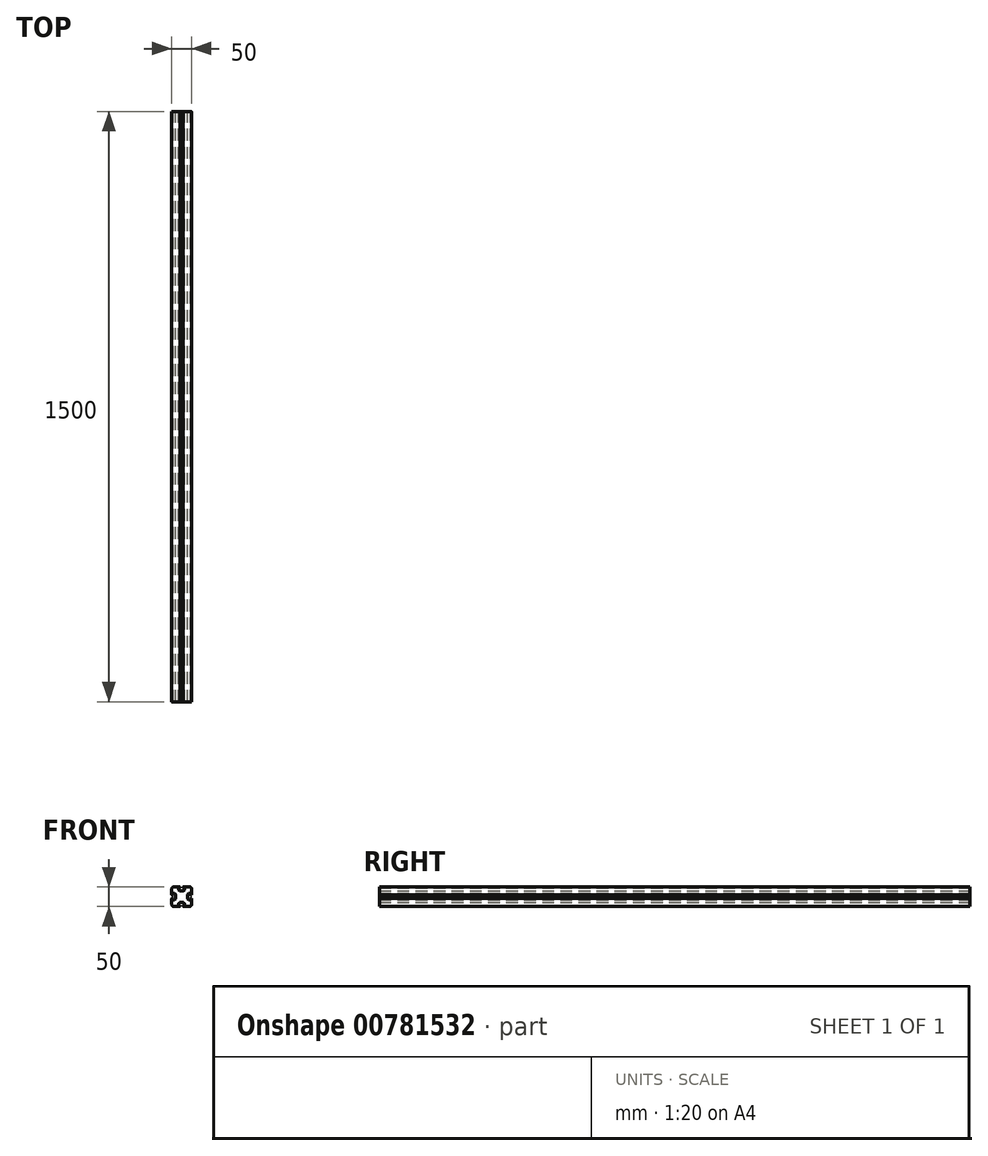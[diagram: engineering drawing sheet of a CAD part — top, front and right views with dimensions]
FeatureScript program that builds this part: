
annotation { "Feature Type Name" : "Feature", "Feature Type Description" : "" }
export const myFeature = defineFeature(function(context is Context, id is Id, definition is map)
    precondition{}
    {
        {
            var Q0;
            Q0=qCreatedBy(makeId("Front.planeOp"),FACE);
            var sketch = newSketch(context, id + "F0", { "sketchPlane" : qUnion([Q0])});
            skLineSegment(sketch, "E0", {"start": v(-15, 0) * mm, "end": v(-15, 5) * mm});
            skLineSegment(sketch, "E1", {"start": v(-15, 5) * mm, "end": v(-18, 8) * mm});
            skLineSegment(sketch, "E2", {"start": v(-18, 8) * mm, "end": v(-22, 8) * mm});
            skLineSegment(sketch, "E3", {"start": v(-22, 8) * mm, "end": v(-22, 4) * mm});
            skLineSegment(sketch, "E4", {"start": v(-22, 4) * mm, "end": v(-25, 4) * mm});
            skLineSegment(sketch, "E5", {"start": v(-25, 4) * mm, "end": v(-25, 25) * mm});
            skLineSegment(sketch, "E6", {"start": v(-25, 25) * mm, "end": v(0, 0) * mm, "construction": true});
            skLineSegment(sketch, "E7.MirrorCS", {"start": v(-4, 25) * mm, "end": v(-25, 25) * mm});
            skLineSegment(sketch, "E8.MirrorCS", {"start": v(-4, 22) * mm, "end": v(-4, 25) * mm});
            skLineSegment(sketch, "E9.MirrorCS", {"start": v(-8, 18) * mm, "end": v(-8, 22) * mm});
            skLineSegment(sketch, "E10.MirrorCS", {"start": v(-5, 15) * mm, "end": v(-8, 18) * mm});
            skLineSegment(sketch, "E11.MirrorCS", {"start": v(-8, 22) * mm, "end": v(-4, 22) * mm});
            skLineSegment(sketch, "E12.MirrorCS", {"start": v(0, 15) * mm, "end": v(-5, 15) * mm});
            skLineSegment(sketch, "E13.1.0", {"start": v(-25, -4) * mm, "end": v(-25, -25) * mm});
            skLineSegment(sketch, "E13.1.1", {"start": v(-22, -4) * mm, "end": v(-25, -4) * mm});
            skLineSegment(sketch, "E13.1.2", {"start": v(-22, -8) * mm, "end": v(-22, -4) * mm});
            skLineSegment(sketch, "E13.1.3", {"start": v(-18, -8) * mm, "end": v(-22, -8) * mm});
            skLineSegment(sketch, "E13.1.4", {"start": v(-15, 0) * mm, "end": v(-15, -5) * mm});
            skLineSegment(sketch, "E13.1.5", {"start": v(-15, -5) * mm, "end": v(-18, -8) * mm});
            skLineSegment(sketch, "E13.1.6", {"start": v(-8, -18) * mm, "end": v(-8, -22) * mm});
            skLineSegment(sketch, "E13.1.7", {"start": v(-5, -15) * mm, "end": v(-8, -18) * mm});
            skLineSegment(sketch, "E13.1.8", {"start": v(0, -15) * mm, "end": v(-5, -15) * mm});
            skLineSegment(sketch, "E13.1.9", {"start": v(-4, -22) * mm, "end": v(-4, -25) * mm});
            skLineSegment(sketch, "E13.1.10", {"start": v(-4, -25) * mm, "end": v(-25, -25) * mm});
            skLineSegment(sketch, "E13.1.11", {"start": v(-8, -22) * mm, "end": v(-4, -22) * mm});
            skLineSegment(sketch, "E13.2.0", {"start": v(4, -25) * mm, "end": v(25, -25) * mm});
            skLineSegment(sketch, "E13.2.1", {"start": v(4, -22) * mm, "end": v(4, -25) * mm});
            skLineSegment(sketch, "E13.2.2", {"start": v(8, -22) * mm, "end": v(4, -22) * mm});
            skLineSegment(sketch, "E13.2.3", {"start": v(8, -18) * mm, "end": v(8, -22) * mm});
            skLineSegment(sketch, "E13.2.4", {"start": v(0, -15) * mm, "end": v(5, -15) * mm});
            skLineSegment(sketch, "E13.2.5", {"start": v(5, -15) * mm, "end": v(8, -18) * mm});
            skLineSegment(sketch, "E13.2.6", {"start": v(18, -8) * mm, "end": v(22, -8) * mm});
            skLineSegment(sketch, "E13.2.7", {"start": v(15, -5) * mm, "end": v(18, -8) * mm});
            skLineSegment(sketch, "E13.2.8", {"start": v(15, 0) * mm, "end": v(15, -5) * mm});
            skLineSegment(sketch, "E13.2.9", {"start": v(22, -4) * mm, "end": v(25, -4) * mm});
            skLineSegment(sketch, "E13.2.10", {"start": v(25, -4) * mm, "end": v(25, -25) * mm});
            skLineSegment(sketch, "E13.2.11", {"start": v(22, -8) * mm, "end": v(22, -4) * mm});
            skLineSegment(sketch, "E13.3.0", {"start": v(25, 4) * mm, "end": v(25, 25) * mm});
            skLineSegment(sketch, "E13.3.1", {"start": v(22, 4) * mm, "end": v(25, 4) * mm});
            skLineSegment(sketch, "E13.3.2", {"start": v(22, 8) * mm, "end": v(22, 4) * mm});
            skLineSegment(sketch, "E13.3.3", {"start": v(18, 8) * mm, "end": v(22, 8) * mm});
            skLineSegment(sketch, "E13.3.4", {"start": v(15, 0) * mm, "end": v(15, 5) * mm});
            skLineSegment(sketch, "E13.3.5", {"start": v(15, 5) * mm, "end": v(18, 8) * mm});
            skLineSegment(sketch, "E13.3.6", {"start": v(8, 18) * mm, "end": v(8, 22) * mm});
            skLineSegment(sketch, "E13.3.7", {"start": v(5, 15) * mm, "end": v(8, 18) * mm});
            skLineSegment(sketch, "E13.3.8", {"start": v(0, 15) * mm, "end": v(5, 15) * mm});
            skLineSegment(sketch, "E13.3.9", {"start": v(4, 22) * mm, "end": v(4, 25) * mm});
            skLineSegment(sketch, "E13.3.10", {"start": v(4, 25) * mm, "end": v(25, 25) * mm});
            skLineSegment(sketch, "E13.3.11", {"start": v(8, 22) * mm, "end": v(4, 22) * mm});
            skPoint(sketch, "E13.center", {"position": v(0, 0) * mm});
            skSolve(sketch);
        }
        {
            var Q0;
            Q0=makeQuery(id+"F0.imprint","IMPRINT",FACE,{"disambiguationData":[TD([[makeQuery(id+"F0.imprint","IMPRINT",EDGE,{"derivedFrom":sQuery(id+"F0.wireOp",EDGE,"E0")}),-1.0]])]});
            extrude(context, id + "F1", {"entities" : qUnion([Q0]), "depth" : 1500 * mm, "offsetDistance" : 25 * mm});
        }
        {
            var Q0;
            Q0=makeQuery(id+"F1.opExtrude","SWEPT_EDGE",EDGE,{"disambiguationData":[OSD([sQuery(id+"F0.wireOp",EDGE,"E13.3.0"),sQuery(id+"F0.wireOp",EDGE,"E13.3.10")])]});
            var Q1;
            Q1=makeQuery(id+"F1.opExtrude","SWEPT_EDGE",EDGE,{"disambiguationData":[OSD([sQuery(id+"F0.wireOp",EDGE,"E13.2.0"),sQuery(id+"F0.wireOp",EDGE,"E13.2.10")])]});
            var Q2;
            Q2=makeQuery(id+"F1.opExtrude","SWEPT_EDGE",EDGE,{"disambiguationData":[OSD([sQuery(id+"F0.wireOp",EDGE,"E5"),sQuery(id+"F0.wireOp",EDGE,"E7.MirrorCS")])]});
            var Q3;
            Q3=makeQuery(id+"F1.opExtrude","SWEPT_EDGE",EDGE,{"disambiguationData":[OSD([sQuery(id+"F0.wireOp",EDGE,"E13.1.0"),sQuery(id+"F0.wireOp",EDGE,"E13.1.10")])]});
            fillet(context, id + "F2", {"entities" : qUnion([Q0, Q1, Q2, Q3]), "radius" : 5 * mm, "tangentPropagation" : true, "allowEdgeOverflow" : false});
        }
        {
            var Q0;
            Q0=makeQuery(id+"F1.opExtrude","SWEPT_EDGE",EDGE,{"disambiguationData":[OSD([sQuery(id+"F0.wireOp",EDGE,"E7.MirrorCS"),sQuery(id+"F0.wireOp",EDGE,"E8.MirrorCS")])]});
            var Q1;
            Q1=makeQuery(id+"F1.opExtrude","SWEPT_EDGE",EDGE,{"disambiguationData":[OSD([sQuery(id+"F0.wireOp",EDGE,"E13.3.9"),sQuery(id+"F0.wireOp",EDGE,"E13.3.10")])]});
            var Q2;
            Q2=makeQuery(id+"F1.opExtrude","SWEPT_EDGE",EDGE,{"disambiguationData":[OSD([sQuery(id+"F0.wireOp",EDGE,"E13.3.9"),sQuery(id+"F0.wireOp",EDGE,"E13.3.11")])]});
            var Q3;
            Q3=makeQuery(id+"F1.opExtrude","SWEPT_EDGE",EDGE,{"disambiguationData":[OSD([sQuery(id+"F0.wireOp",EDGE,"E13.3.6"),sQuery(id+"F0.wireOp",EDGE,"E13.3.7")])]});
            var Q4;
            Q4=makeQuery(id+"F1.opExtrude","SWEPT_EDGE",EDGE,{"disambiguationData":[OSD([sQuery(id+"F0.wireOp",EDGE,"E13.3.7"),sQuery(id+"F0.wireOp",EDGE,"E13.3.8")])]});
            var Q5;
            Q5=makeQuery(id+"F1.opExtrude","SWEPT_EDGE",EDGE,{"disambiguationData":[OSD([sQuery(id+"F0.wireOp",EDGE,"E9.MirrorCS"),sQuery(id+"F0.wireOp",EDGE,"E10.MirrorCS")])]});
            var Q6;
            Q6=makeQuery(id+"F1.opExtrude","SWEPT_EDGE",EDGE,{"disambiguationData":[OSD([sQuery(id+"F0.wireOp",EDGE,"E10.MirrorCS"),sQuery(id+"F0.wireOp",EDGE,"E12.MirrorCS")])]});
            var Q7;
            Q7=makeQuery(id+"F1.opExtrude","SWEPT_EDGE",EDGE,{"disambiguationData":[OSD([sQuery(id+"F0.wireOp",EDGE,"E9.MirrorCS"),sQuery(id+"F0.wireOp",EDGE,"E11.MirrorCS")])]});
            var Q8;
            Q8=makeQuery(id+"F1.opExtrude","SWEPT_EDGE",EDGE,{"disambiguationData":[OSD([sQuery(id+"F0.wireOp",EDGE,"E13.3.4"),sQuery(id+"F0.wireOp",EDGE,"E13.3.5")])]});
            var Q9;
            Q9=makeQuery(id+"F1.opExtrude","SWEPT_EDGE",EDGE,{"disambiguationData":[OSD([sQuery(id+"F0.wireOp",EDGE,"E13.2.7"),sQuery(id+"F0.wireOp",EDGE,"E13.2.8")])]});
            var Q10;
            Q10=makeQuery(id+"F1.opExtrude","SWEPT_EDGE",EDGE,{"disambiguationData":[OSD([sQuery(id+"F0.wireOp",EDGE,"E13.3.2"),sQuery(id+"F0.wireOp",EDGE,"E13.3.3")])]});
            var Q11;
            Q11=makeQuery(id+"F1.opExtrude","SWEPT_EDGE",EDGE,{"disambiguationData":[OSD([sQuery(id+"F0.wireOp",EDGE,"E13.3.1"),sQuery(id+"F0.wireOp",EDGE,"E13.3.2")])]});
            var Q12;
            Q12=makeQuery(id+"F1.opExtrude","SWEPT_EDGE",EDGE,{"disambiguationData":[OSD([sQuery(id+"F0.wireOp",EDGE,"E13.3.0"),sQuery(id+"F0.wireOp",EDGE,"E13.3.1")])]});
            var Q13;
            Q13=makeQuery(id+"F1.opExtrude","SWEPT_EDGE",EDGE,{"disambiguationData":[OSD([sQuery(id+"F0.wireOp",EDGE,"E13.3.6"),sQuery(id+"F0.wireOp",EDGE,"E13.3.11")])]});
            var Q14;
            Q14=makeQuery(id+"F1.opExtrude","SWEPT_EDGE",EDGE,{"disambiguationData":[OSD([sQuery(id+"F0.wireOp",EDGE,"E8.MirrorCS"),sQuery(id+"F0.wireOp",EDGE,"E11.MirrorCS")])]});
            var Q15;
            Q15=makeQuery(id+"F1.opExtrude","SWEPT_EDGE",EDGE,{"disambiguationData":[OSD([sQuery(id+"F0.wireOp",EDGE,"E13.2.6"),sQuery(id+"F0.wireOp",EDGE,"E13.2.7")])]});
            var Q16;
            Q16=makeQuery(id+"F1.opExtrude","SWEPT_EDGE",EDGE,{"disambiguationData":[OSD([sQuery(id+"F0.wireOp",EDGE,"E13.2.6"),sQuery(id+"F0.wireOp",EDGE,"E13.2.11")])]});
            var Q17;
            Q17=makeQuery(id+"F1.opExtrude","SWEPT_EDGE",EDGE,{"disambiguationData":[OSD([sQuery(id+"F0.wireOp",EDGE,"E13.2.9"),sQuery(id+"F0.wireOp",EDGE,"E13.2.11")])]});
            var Q18;
            Q18=makeQuery(id+"F1.opExtrude","SWEPT_EDGE",EDGE,{"disambiguationData":[OSD([sQuery(id+"F0.wireOp",EDGE,"E13.2.9"),sQuery(id+"F0.wireOp",EDGE,"E13.2.10")])]});
            var Q19;
            Q19=makeQuery(id+"F1.opExtrude","SWEPT_EDGE",EDGE,{"disambiguationData":[OSD([sQuery(id+"F0.wireOp",EDGE,"E13.2.0"),sQuery(id+"F0.wireOp",EDGE,"E13.2.1")])]});
            var Q20;
            Q20=makeQuery(id+"F1.opExtrude","SWEPT_EDGE",EDGE,{"disambiguationData":[OSD([sQuery(id+"F0.wireOp",EDGE,"E13.2.2"),sQuery(id+"F0.wireOp",EDGE,"E13.2.3")])]});
            var Q21;
            Q21=makeQuery(id+"F1.opExtrude","SWEPT_EDGE",EDGE,{"disambiguationData":[OSD([sQuery(id+"F0.wireOp",EDGE,"E13.1.6"),sQuery(id+"F0.wireOp",EDGE,"E13.1.7")])]});
            var Q22;
            Q22=makeQuery(id+"F1.opExtrude","SWEPT_EDGE",EDGE,{"disambiguationData":[OSD([sQuery(id+"F0.wireOp",EDGE,"E13.1.7"),sQuery(id+"F0.wireOp",EDGE,"E13.1.8")])]});
            var Q23;
            Q23=makeQuery(id+"F1.opExtrude","SWEPT_EDGE",EDGE,{"disambiguationData":[OSD([sQuery(id+"F0.wireOp",EDGE,"E13.1.9"),sQuery(id+"F0.wireOp",EDGE,"E13.1.11")])]});
            var Q24;
            Q24=makeQuery(id+"F1.opExtrude","SWEPT_EDGE",EDGE,{"disambiguationData":[OSD([sQuery(id+"F0.wireOp",EDGE,"E13.1.9"),sQuery(id+"F0.wireOp",EDGE,"E13.1.10")])]});
            var Q25;
            Q25=makeQuery(id+"F1.opExtrude","SWEPT_EDGE",EDGE,{"disambiguationData":[OSD([sQuery(id+"F0.wireOp",EDGE,"E13.1.6"),sQuery(id+"F0.wireOp",EDGE,"E13.1.11")])]});
            var Q26;
            Q26=makeQuery(id+"F1.opExtrude","SWEPT_EDGE",EDGE,{"disambiguationData":[OSD([sQuery(id+"F0.wireOp",EDGE,"E13.3.3"),sQuery(id+"F0.wireOp",EDGE,"E13.3.5")])]});
            var Q27;
            Q27=makeQuery(id+"F1.opExtrude","SWEPT_EDGE",EDGE,{"disambiguationData":[OSD([sQuery(id+"F0.wireOp",EDGE,"E13.2.3"),sQuery(id+"F0.wireOp",EDGE,"E13.2.5")])]});
            var Q28;
            Q28=makeQuery(id+"F1.opExtrude","SWEPT_EDGE",EDGE,{"disambiguationData":[OSD([sQuery(id+"F0.wireOp",EDGE,"E13.2.4"),sQuery(id+"F0.wireOp",EDGE,"E13.2.5")])]});
            var Q29;
            Q29=makeQuery(id+"F1.opExtrude","SWEPT_EDGE",EDGE,{"disambiguationData":[OSD([sQuery(id+"F0.wireOp",EDGE,"E13.2.1"),sQuery(id+"F0.wireOp",EDGE,"E13.2.2")])]});
            var Q30;
            Q30=makeQuery(id+"F1.opExtrude","SWEPT_EDGE",EDGE,{"disambiguationData":[OSD([sQuery(id+"F0.wireOp",EDGE,"E4"),sQuery(id+"F0.wireOp",EDGE,"E5")])]});
            var Q31;
            Q31=makeQuery(id+"F1.opExtrude","SWEPT_EDGE",EDGE,{"disambiguationData":[OSD([sQuery(id+"F0.wireOp",EDGE,"E3"),sQuery(id+"F0.wireOp",EDGE,"E4")])]});
            var Q32;
            Q32=makeQuery(id+"F1.opExtrude","SWEPT_EDGE",EDGE,{"disambiguationData":[OSD([sQuery(id+"F0.wireOp",EDGE,"E2"),sQuery(id+"F0.wireOp",EDGE,"E3")])]});
            var Q33;
            Q33=makeQuery(id+"F1.opExtrude","SWEPT_EDGE",EDGE,{"disambiguationData":[OSD([sQuery(id+"F0.wireOp",EDGE,"E1"),sQuery(id+"F0.wireOp",EDGE,"E2")])]});
            var Q34;
            Q34=makeQuery(id+"F1.opExtrude","SWEPT_EDGE",EDGE,{"disambiguationData":[OSD([sQuery(id+"F0.wireOp",EDGE,"E13.1.1"),sQuery(id+"F0.wireOp",EDGE,"E13.1.2")])]});
            var Q35;
            Q35=makeQuery(id+"F1.opExtrude","SWEPT_EDGE",EDGE,{"disambiguationData":[OSD([sQuery(id+"F0.wireOp",EDGE,"E13.1.0"),sQuery(id+"F0.wireOp",EDGE,"E13.1.1")])]});
            var Q36;
            Q36=makeQuery(id+"F1.opExtrude","SWEPT_EDGE",EDGE,{"disambiguationData":[OSD([sQuery(id+"F0.wireOp",EDGE,"E13.1.3"),sQuery(id+"F0.wireOp",EDGE,"E13.1.5")])]});
            var Q37;
            Q37=makeQuery(id+"F1.opExtrude","SWEPT_EDGE",EDGE,{"disambiguationData":[OSD([sQuery(id+"F0.wireOp",EDGE,"E0"),sQuery(id+"F0.wireOp",EDGE,"E1")])]});
            var Q38;
            Q38=makeQuery(id+"F1.opExtrude","SWEPT_EDGE",EDGE,{"disambiguationData":[OSD([sQuery(id+"F0.wireOp",EDGE,"E13.1.4"),sQuery(id+"F0.wireOp",EDGE,"E13.1.5")])]});
            var Q39;
            Q39=makeQuery(id+"F1.opExtrude","SWEPT_EDGE",EDGE,{"disambiguationData":[OSD([sQuery(id+"F0.wireOp",EDGE,"E13.1.2"),sQuery(id+"F0.wireOp",EDGE,"E13.1.3")])]});
            fillet(context, id + "F3", {"entities" : qUnion([Q0, Q1, Q2, Q3, Q4, Q5, Q6, Q7, Q8, Q9, Q10, Q11, Q12, Q13, Q14, Q15, Q16, Q17, Q18, Q19, Q20, Q21, Q22, Q23, Q24, Q25, Q26, Q27, Q28, Q29, Q30, Q31, Q32, Q33, Q34, Q35, Q36, Q37, Q38, Q39]), "radius" : 1 * mm, "tangentPropagation" : true, "allowEdgeOverflow" : false});
        }
    });
